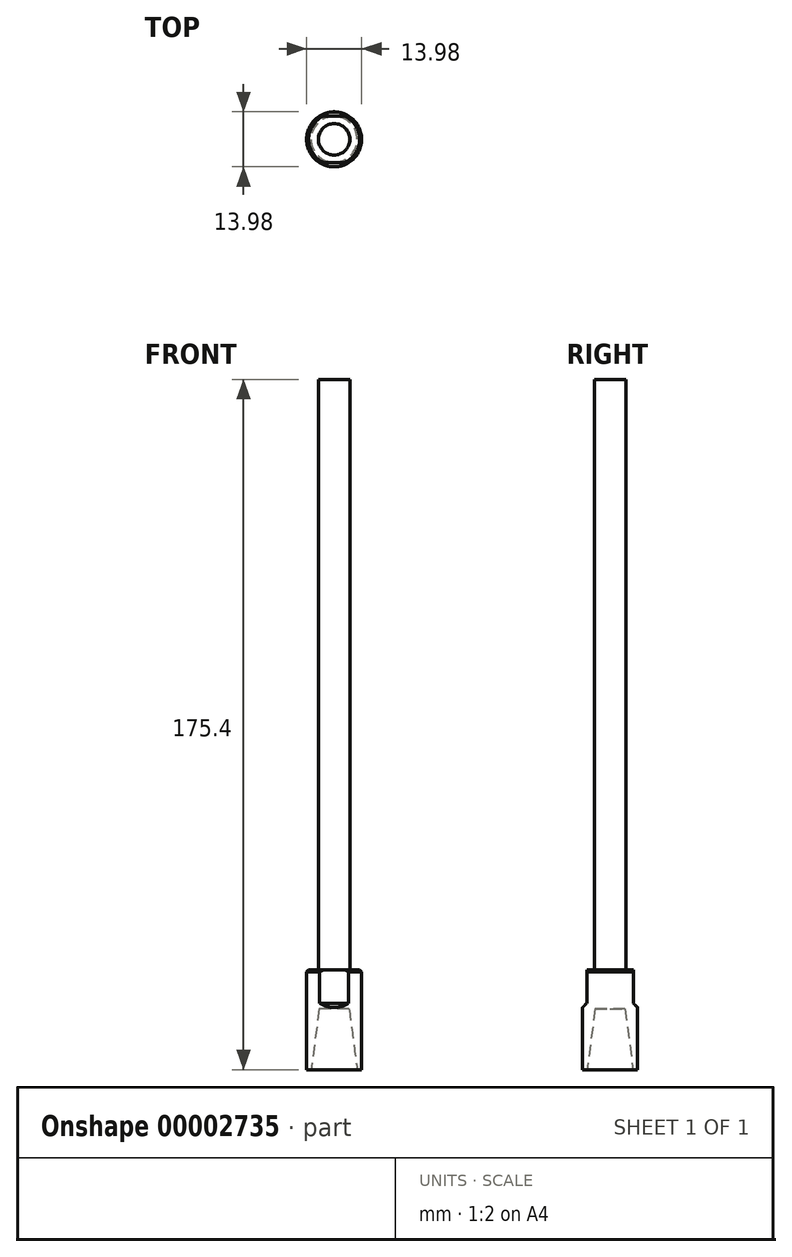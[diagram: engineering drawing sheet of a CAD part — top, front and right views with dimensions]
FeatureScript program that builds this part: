
annotation { "Feature Type Name" : "Feature", "Feature Type Description" : "" }
export const myFeature = defineFeature(function(context is Context, id is Id, definition is map)
    precondition{}
    {
        {
            var Q0;
            Q0=qCreatedBy(makeId("Top.planeOp"),FACE);
            var sketch = newSketch(context, id + "F0", { "sketchPlane" : qUnion([Q0])});
            skCircle(sketch, "E0", {"center": v(0, 0) * mm, "radius": 4 * mm});
            skSolve(sketch);
        }
        {
            var Q0;
            Q0=makeQuery(id+"F0.imprint","IMPRINT",FACE,{"disambiguationData":[TD([[makeQuery(id+"F0.imprint","IMPRINT",EDGE,{"derivedFrom":sQuery(id+"F0.wireOp",EDGE,"E0")}),1.0]])]});
            extrude(context, id + "F1", {"entities" : qUnion([Q0]), "depth" : 150 * mm});
        }
        {
            var Q0;
            Q0=makeQuery(id+"F1.opExtrude","CAP_FACE",FACE,{"disambiguationData":[OSD([sQuery(id+"F0.wireOp",EDGE,"E0")])],"isStart":true});
            var sketch = newSketch(context, id + "F2", { "sketchPlane" : qUnion([Q0])});
            skCircle(sketch, "E1", {"center": v(0, 0) * mm, "radius": 6.99 * mm});
            skSolve(sketch);
        }
        {
            var Q0;
            {var subQ0=makeQuery(id+"F2.imprint","IMPRINT",EDGE,{"derivedFrom":makeQuery(id+"F1.opExtrude","CAP_EDGE",EDGE,{"disambiguationData":[OSD([sQuery(id+"F0.wireOp",EDGE,"E0")])],"isStart":true})});Q0=qUnion([makeQuery(id+"F2.imprint","IMPRINT",FACE,{"disambiguationData":[TD([[makeQuery(id+"F2.imprint","IMPRINT",EDGE,{"derivedFrom":sQuery(id+"F2.wireOp",EDGE,"E1")}),1.0]])]}),makeQuery(id+"F2.imprint","IMPRINT",FACE,{"disambiguationData":[TD([[subQ0,-1.0]])]})]);}
            extrude(context, id + "F3", {"entities" : qUnion([Q0]), "operationType" : NewBodyOperationType.ADD, "depth" : 25.4 * mm});
        }
        {
            var Q0;
            Q0=qCreatedBy(makeId("Right.planeOp"),FACE);
            var sketch = newSketch(context, id + "F4", { "sketchPlane" : qUnion([Q0])});
            skLineSegment(sketch, "E2", {"start": v(0, -25.4) * mm, "end": v(5.84, -25.4) * mm});
            skLineSegment(sketch, "E3", {"start": v(5.84, -25.4) * mm, "end": v(3.8, -9.9) * mm});
            skLineSegment(sketch, "E4", {"start": v(3.8, -9.9) * mm, "end": v(0, -9.9) * mm});
            skLineSegment(sketch, "E5", {"start": v(0, -9.9) * mm, "end": v(0, -25.4) * mm});
            skLineSegment(sketch, "E6", {"start": v(0, 0) * mm, "end": v(0, -25.4) * mm, "construction": true});
            skSolve(sketch);
        }
        {
            var Q0;
            Q0=qCreatedBy(makeId("Right.planeOp"),FACE);
            var sketch = newSketch(context, id + "F5", { "sketchPlane" : qUnion([Q0])});
            skLineSegment(sketch, "E7", {"start": v(0, 0) * mm, "end": v(0, -33.44) * mm, "construction": true});
            skSolve(sketch);
        }
        {
            var Q0;
            Q0=makeQuery(id+"F4.imprint","IMPRINT",FACE,{"disambiguationData":[TD([[makeQuery(id+"F4.imprint","IMPRINT",EDGE,{"derivedFrom":sQuery(id+"F4.wireOp",EDGE,"E2")}),1.0]])]});
            var Q1;
            Q1=sQuery(id+"F5.wireOp",EDGE,"E7");
            revolve(context, id + "F6", {"operationType" : NewBodyOperationType.REMOVE, "entities" : qUnion([Q0]), "axis" : qUnion([Q1]), "revolveType" : RevolveType.FULL});
        }
        {
            var Q0;
            Q0=qCreatedBy(makeId("Right.planeOp"),FACE);
            var sketch = newSketch(context, id + "F7", { "sketchPlane" : qUnion([Q0])});
            skLineSegment(sketch, "E8.bottom", {"start": v(5.93, 0) * mm, "end": v(9.15, 0) * mm});
            skLineSegment(sketch, "E8.top", {"start": v(5.93, -9.53) * mm, "end": v(9.15, -9.53) * mm});
            skLineSegment(sketch, "E8.left", {"start": v(5.93, 0) * mm, "end": v(5.93, -9.53) * mm});
            skLineSegment(sketch, "E8.right", {"start": v(9.15, 0) * mm, "end": v(9.15, -9.53) * mm});
            skLineSegment(sketch, "E9.bottom", {"start": v(-5.93, 0) * mm, "end": v(-9.17, 0) * mm});
            skLineSegment(sketch, "E9.top", {"start": v(-5.93, -9.53) * mm, "end": v(-9.17, -9.53) * mm});
            skLineSegment(sketch, "E9.left", {"start": v(-5.93, 0) * mm, "end": v(-5.93, -9.53) * mm});
            skLineSegment(sketch, "E9.right", {"start": v(-9.17, 0) * mm, "end": v(-9.17, -9.53) * mm});
            skSolve(sketch);
        }
        {
            var Q0;
            {Q0=qUnion([makeQuery(id+"F7.imprint","IMPRINT",FACE,{"disambiguationData":[TD([[makeQuery(id+"F7.imprint","IMPRINT",EDGE,{"derivedFrom":sQuery(id+"F7.wireOp",EDGE,"E8.bottom")}),-1.0]])]}),makeQuery(id+"F7.imprint","IMPRINT",FACE,{"disambiguationData":[TD([[makeQuery(id+"F7.imprint","IMPRINT",EDGE,{"derivedFrom":sQuery(id+"F7.wireOp",EDGE,"E9.bottom")}),1.0]])]})]);}
            extrude(context, id + "F8", {"entities" : qUnion([Q0]), "operationType" : NewBodyOperationType.REMOVE, "endBound" : BoundingType.SYMMETRIC, "oppositeDirection" : true, "depth" : 25.4 * mm});
        }
        {
            var Q0;
            Q0=makeQuery(id+"F8.boolean.opBoolean","SPLIT",EDGE,{"disambiguationData":[OD(1.0)],"derivedFrom":makeQuery(id+"F3.opExtrude","CAP_EDGE",EDGE,{"disambiguationData":[OSD([sQuery(id+"F2.wireOp",EDGE,"E1")])],"isStart":true})});
            var Q1;
            Q1=makeQuery(id+"F8.boolean.opBoolean","SPLIT",EDGE,{"disambiguationData":[OD(0.0)],"derivedFrom":makeQuery(id+"F3.opExtrude","CAP_EDGE",EDGE,{"disambiguationData":[OSD([sQuery(id+"F2.wireOp",EDGE,"E1")])],"isStart":true})});
            chamfer(context, id + "F9", {"entities" : qUnion([Q0, Q1]), "width" : 0.5 * mm});
        }
        {
            var Q0;
            Q0=makeQuery(id+"F8.boolean.opBoolean","COPY",EDGE,{"derivedFrom":makeQuery(id+"F8.opExtrude","SWEPT_EDGE",EDGE,{"disambiguationData":[OSD([sQuery(id+"F7.wireOp",EDGE,"E8.top"),sQuery(id+"F7.wireOp",EDGE,"E8.left")])]})});
            var Q1;
            Q1=makeQuery(id+"F8.boolean.opBoolean","COPY",EDGE,{"derivedFrom":makeQuery(id+"F8.opExtrude","SWEPT_EDGE",EDGE,{"disambiguationData":[OSD([sQuery(id+"F7.wireOp",EDGE,"E9.top"),sQuery(id+"F7.wireOp",EDGE,"E9.left")])]})});
            chamfer(context, id + "F10", {"entities" : qUnion([Q0, Q1]), "width" : 1.02 * mm, "tangentPropagation" : true});
        }
    });
